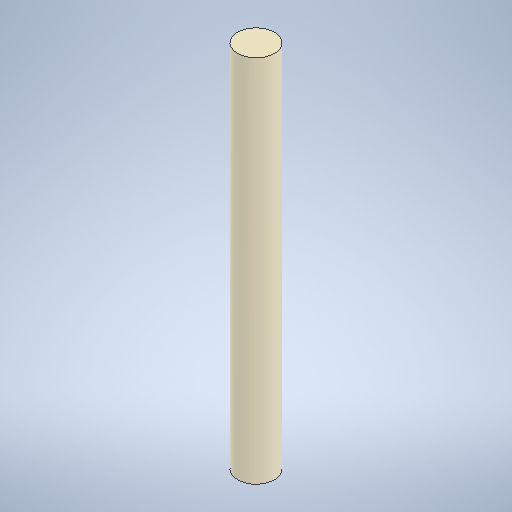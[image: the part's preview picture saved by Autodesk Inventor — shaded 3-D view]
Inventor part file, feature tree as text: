
AUTODESK INVENTOR PART (.ipt)
format: ipt  version: 2025.2 (Build 292293000, 293)  size: 229,376 bytes
history: native  units: in
note: dims shown in document units (in); Inventor stores cm internally (conversion verified against a paired STEP export)
features: extrude x1, sketch x1
ambient origin geometry x8: Origin, YZ Plane, XZ Plane, XY Plane, X Axis, Y Axis, Z Axis, Center Point
bodies: Solid1 (feature_tree)
feature tree (2):
  extrude  "Extrusion1"  Depth=5.0in TaperAngle=0.0deg
  sketch  "Sketch1"  dims[d0=0.5in d1=5.0in d2=0.0in]
